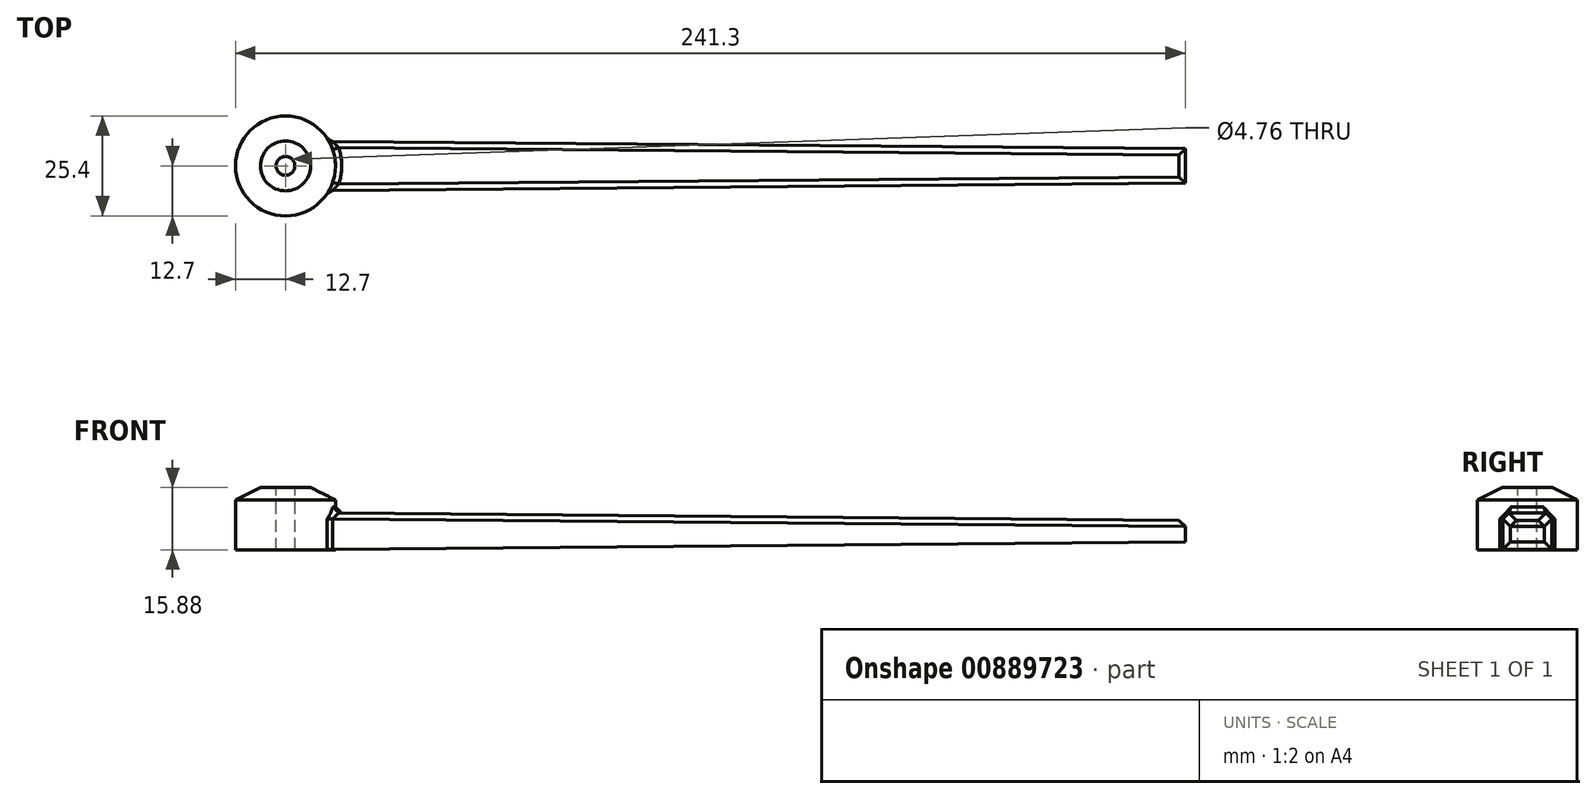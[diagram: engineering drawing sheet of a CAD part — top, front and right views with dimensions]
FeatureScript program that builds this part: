
annotation { "Feature Type Name" : "Feature", "Feature Type Description" : "" }
export const myFeature = defineFeature(function(context is Context, id is Id, definition is map)
    precondition{}
    {
        {
            var Q0;
            Q0=qCreatedBy(makeId("Top.planeOp"),FACE);
            var sketch = newSketch(context, id + "F0", { "sketchPlane" : qUnion([Q0])});
            skCircle(sketch, "E0", {"center": v(0, 0) * mm, "radius": 12.7 * mm});
            skSolve(sketch);
        }
        {
            var Q0;
            Q0=makeQuery(id+"F0.imprint","IMPRINT",FACE,{"disambiguationData":[TD([[makeQuery(id+"F0.imprint","IMPRINT",EDGE,{"derivedFrom":sQuery(id+"F0.wireOp",EDGE,"E0")}),1.0]])]});
            extrude(context, id + "F1", {"entities" : qUnion([Q0]), "depth" : 15.88 * mm, "offsetDistance" : 25.4 * mm});
        }
        {
            var Q0;
            Q0=qCreatedBy(makeId("Right.planeOp"),FACE);
            var sketch = newSketch(context, id + "F2", { "sketchPlane" : qUnion([Q0])});
            skLineSegment(sketch, "E1.bottom", {"start": v(-6.35, 0) * mm, "end": v(6.35, 0) * mm});
            skLineSegment(sketch, "E1.top", {"start": v(-6.35, 9.53) * mm, "end": v(6.35, 9.53) * mm});
            skLineSegment(sketch, "E1.left", {"start": v(-6.35, 0) * mm, "end": v(-6.35, 9.53) * mm});
            skLineSegment(sketch, "E1.right", {"start": v(6.35, 0) * mm, "end": v(6.35, 9.53) * mm});
            skSolve(sketch);
        }
        {
            var Q0;
            Q0 = qSketchRegion(id + "F2", true);
            extrude(context, id + "F3", {"entities" : qUnion([Q0]), "operationType" : NewBodyOperationType.ADD, "depth" : 228.6 * mm, "offsetDistance" : 25.4 * mm, "hasDraft" : true, "draftAngle" : .5 * degree, "draftPullDirection" : true});
        }
        {
            var Q0;
            Q0=makeQuery(id+"F1.opExtrude","CAP_EDGE",EDGE,{"disambiguationData":[OSD([sQuery(id+"F0.wireOp",EDGE,"E0")])],"isStart":false});
            chamfer(context, id + "F4", {"entities" : qUnion([Q0]), "chamferType" : ChamferType.TWO_OFFSETS, "width1" : 3.17 * mm, "oppositeDirection" : true, "width2" : 6.35 * mm, "tangentPropagation" : true});
        }
        {
            var Q0;
            Q0=makeQuery(id+"F1.opExtrude","CAP_FACE",FACE,{"disambiguationData":[OSD([sQuery(id+"F0.wireOp",EDGE,"E0")])],"isStart":false});
            var sketch = newSketch(context, id + "F5", { "sketchPlane" : qUnion([Q0])});
            skCircle(sketch, "E2", {"center": v(0, 0) * mm, "radius": 2.38 * mm});
            skSolve(sketch);
        }
        {
            var Q0;
            Q0=makeQuery(id+"F5.imprint","IMPRINT",FACE,{"disambiguationData":[TD([[makeQuery(id+"F5.imprint","IMPRINT",EDGE,{"derivedFrom":sQuery(id+"F5.wireOp",EDGE,"E2")}),1.0]])]});
            extrude(context, id + "F6", {"entities" : qUnion([Q0]), "operationType" : NewBodyOperationType.REMOVE, "endBound" : BoundingType.THROUGH_ALL, "oppositeDirection" : true, "depth" : 25.4 * mm, "offsetDistance" : 25.4 * mm});
        }
        {
            var Q0;
            Q0=makeQuery(id+"F3.opExtrude","SWEPT_FACE",FACE,{"disambiguationData":[OSD([sQuery(id+"F2.wireOp",EDGE,"E1.top")])]});
            chamfer(context, id + "F7", {"entities" : qUnion([Q0]), "width" : 1.59 * mm, "tangentPropagation" : true});
        }
    });
